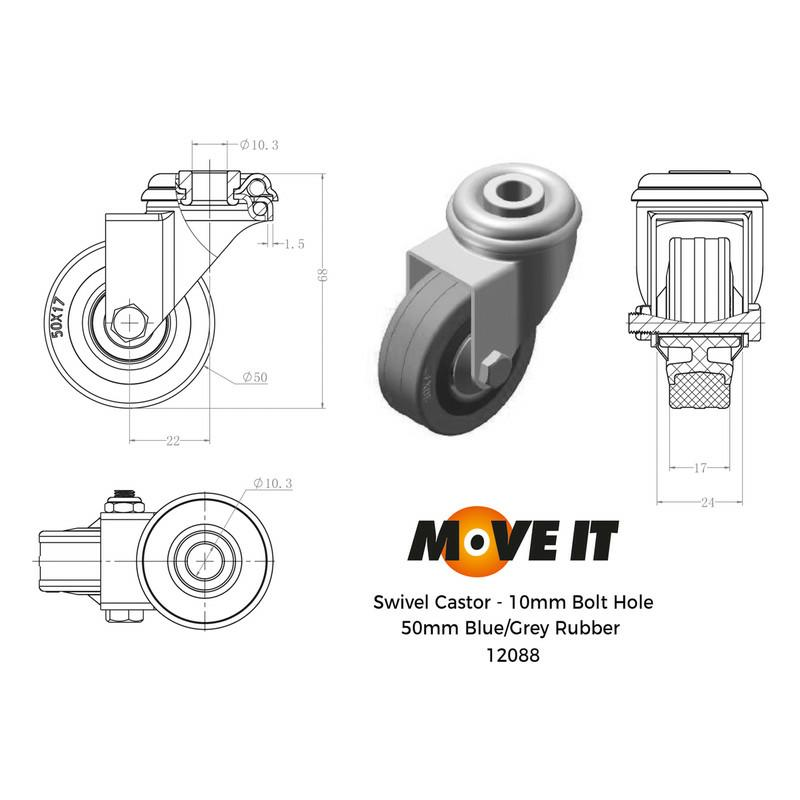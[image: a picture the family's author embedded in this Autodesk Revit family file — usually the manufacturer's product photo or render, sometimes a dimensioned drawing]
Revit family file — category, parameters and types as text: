
# Revit family: ThinkingWall Combi Shelf
name_source: partatom
category: Generic Models
units: mm (PartAtom-declared; Revit-internal decimal feet)

## family parameters
Always vertical = Yes
Can host rebar = No
Cut with Voids When Loaded = No
Maintain Annotation Orientation = No
Part Type = Normal
Room Calculation Point = No
Round Connector Dimension = Use Diameter
Shared = No
Work Plane-Based = No

## types (1)
- ThinkingWall® Combi Shelf
    Acoustic Colour = <By Category>
    Default Elevation = 0 mm  [stored 0 ft]
    Description = Mobile freestanding storage unit with shelves above. Part of the ThinkingWall® range for flexible breakout and meeting spaces.
    Door Colour = <By Category>
    Length = 1200 mm
    Manufacturer = Logovisual LTD
    Model = ThinkingWall® Combi Shelf
    No of Slat = 30
    Shelf Colour = <By Category>
    Steel Colour = <By Category>
    URL = https://www.logovisual.com

note: [stored X ft] marks values corroborated as IEEE doubles in the binary element streams (Revit-internal decimal feet)

## geometry (parser evidence)
native form markers: Sweep x15
no freeform markers — native parametric forms only
